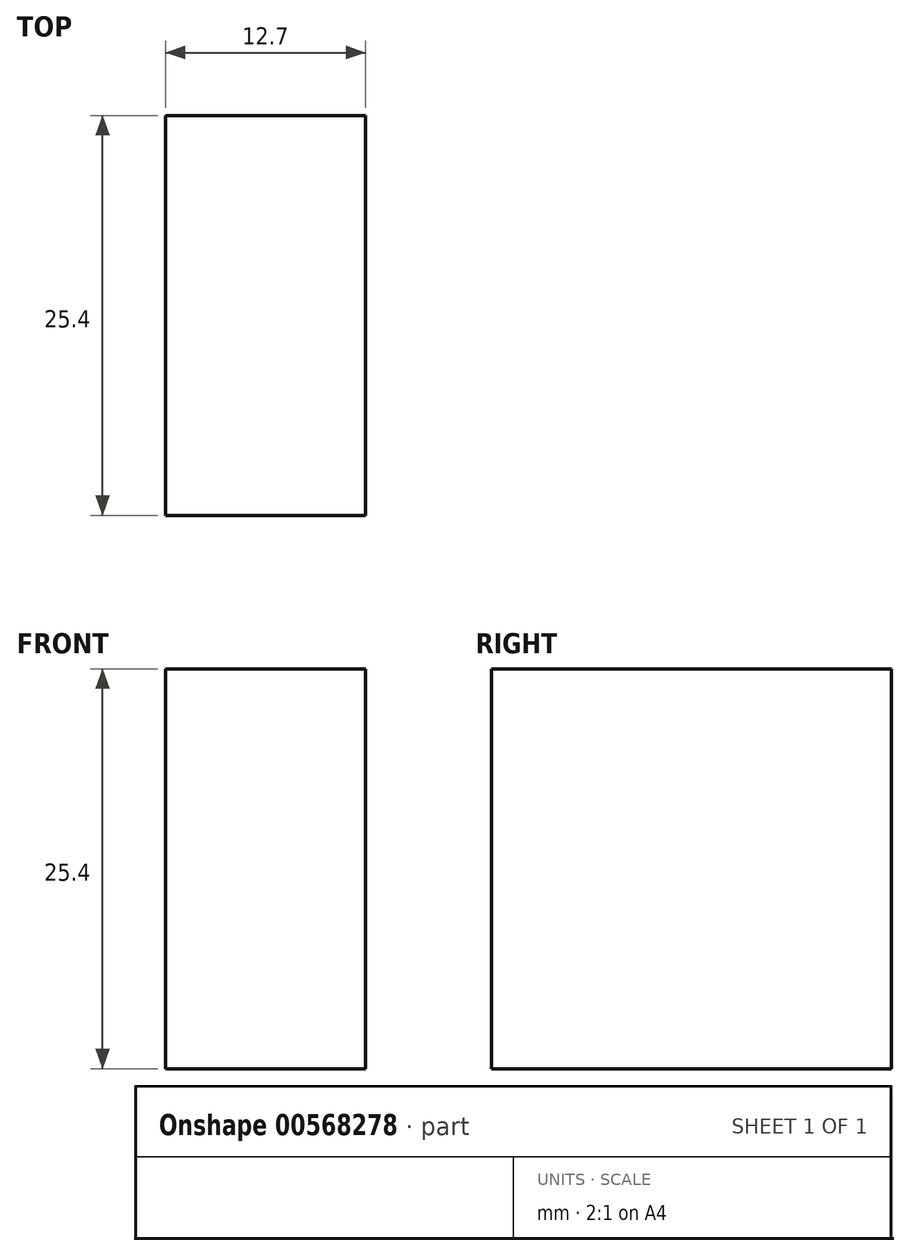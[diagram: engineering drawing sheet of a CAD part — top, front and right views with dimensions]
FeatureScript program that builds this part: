
annotation { "Feature Type Name" : "Feature", "Feature Type Description" : "" }
export const myFeature = defineFeature(function(context is Context, id is Id, definition is map)
    precondition{}
    {
        {
            var Q0;
            Q0=qCreatedBy(makeId("Right.planeOp"),FACE);
            var sketch = newSketch(context, id + "F0", { "sketchPlane" : qUnion([Q0])});
            skLineSegment(sketch, "E0", {"start": v(0, 0) * mm, "end": v(0, 25.4) * mm});
            skLineSegment(sketch, "E1", {"start": v(0, 25.4) * mm, "end": v(25.4, 25.4) * mm});
            skLineSegment(sketch, "E2", {"start": v(25.4, 25.4) * mm, "end": v(25.4, 0) * mm});
            skLineSegment(sketch, "E3", {"start": v(25.4, 0) * mm, "end": v(0, 0) * mm});
            skSolve(sketch);
        }
        {
            var Q0;
            Q0 = qSketchRegion(id + "F0", true);
            extrude(context, id + "F1", {"entities" : qUnion([Q0]), "depth" : 12.7 * mm, "offsetDistance" : 25.4 * mm});
        }
    });
